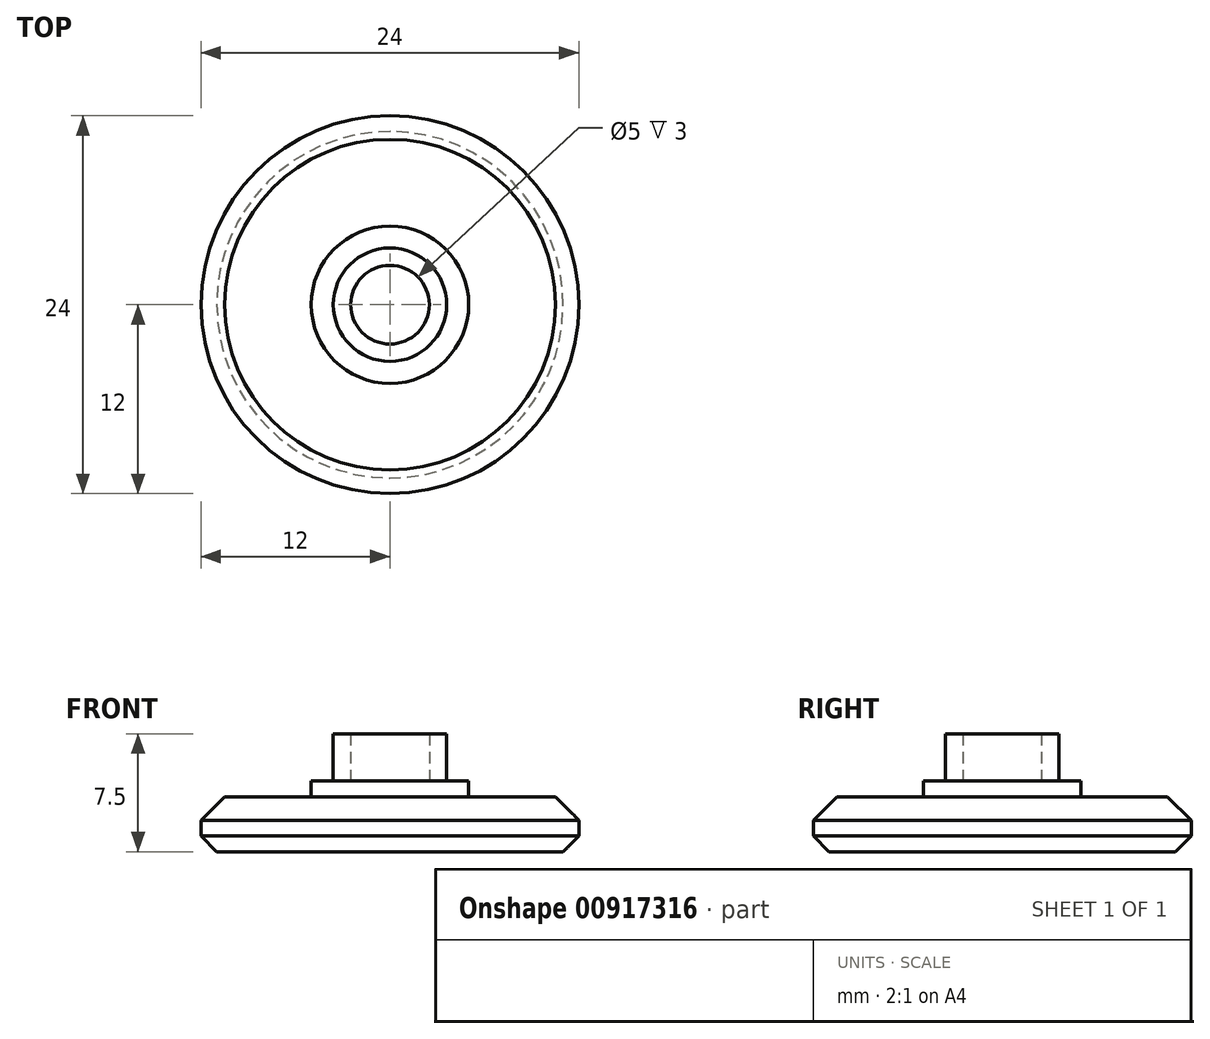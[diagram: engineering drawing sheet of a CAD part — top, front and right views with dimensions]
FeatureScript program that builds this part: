
annotation { "Feature Type Name" : "Feature", "Feature Type Description" : "" }
export const myFeature = defineFeature(function(context is Context, id is Id, definition is map)
    precondition{}
    {
        {
            var Q0;
            Q0=qCreatedBy(makeId("Top.planeOp"),FACE);
            var sketch = newSketch(context, id + "F0", { "sketchPlane" : qUnion([Q0])});
            skCircle(sketch, "E0", {"center": v(0, 0) * mm, "radius": 12 * mm});
            skCircle(sketch, "E1", {"center": v(0, 0) * mm, "radius": 11 * mm});
            skCircle(sketch, "E2", {"center": v(0, 0) * mm, "radius": 4.1 * mm});
            skCircle(sketch, "E3", {"center": v(0, 0) * mm, "radius": 3 * mm});
            skCircle(sketch, "E4", {"center": v(0, 0) * mm, "radius": 5 * mm});
            skSolve(sketch);
        }
        {
            var Q0;
            Q0=makeQuery(id+"F0.imprint","IMPRINT",FACE,{"disambiguationData":[TD([[makeQuery(id+"F0.imprint","IMPRINT",EDGE,{"derivedFrom":sQuery(id+"F0.wireOp",EDGE,"E0")}),1.0]])]});
            var Q1;
            Q1=makeQuery(id+"F0.imprint","IMPRINT",FACE,{"disambiguationData":[TD([[makeQuery(id+"F0.imprint","IMPRINT",EDGE,{"derivedFrom":sQuery(id+"F0.wireOp",EDGE,"E1")}),1.0]])]});
            var Q2;
            Q2=makeQuery(id+"F0.imprint","IMPRINT",FACE,{"disambiguationData":[TD([[makeQuery(id+"F0.imprint","IMPRINT",EDGE,{"derivedFrom":sQuery(id+"F0.wireOp",EDGE,"E3")}),1.0]])]});
            var Q3;
            Q3=makeQuery(id+"F0.imprint","IMPRINT",FACE,{"disambiguationData":[TD([[makeQuery(id+"F0.imprint","IMPRINT",EDGE,{"derivedFrom":sQuery(id+"F0.wireOp",EDGE,"E2")}),1.0]])]});
            var Q4;
            Q4=makeQuery(id+"F0.imprint","IMPRINT",FACE,{"disambiguationData":[TD([[makeQuery(id+"F0.imprint","IMPRINT",EDGE,{"derivedFrom":sQuery(id+"F0.wireOp",EDGE,"E2")}),-1.0]])]});
            extrude(context, id + "F1", {"entities" : qUnion([Q0, Q1, Q2, Q3, Q4]), "depth" : 2 * mm, "offsetDistance" : 25 * mm});
        }
        {
            var Q0;
            Q0=makeQuery(id+"F0.imprint","IMPRINT",FACE,{"disambiguationData":[TD([[makeQuery(id+"F0.imprint","IMPRINT",EDGE,{"derivedFrom":sQuery(id+"F0.wireOp",EDGE,"E1")}),1.0]])]});
            var Q1;
            Q1=makeQuery(id+"F0.imprint","IMPRINT",FACE,{"disambiguationData":[TD([[makeQuery(id+"F0.imprint","IMPRINT",EDGE,{"derivedFrom":sQuery(id+"F0.wireOp",EDGE,"E2")}),1.0]])]});
            var Q2;
            Q2=makeQuery(id+"F0.imprint","IMPRINT",FACE,{"disambiguationData":[TD([[makeQuery(id+"F0.imprint","IMPRINT",EDGE,{"derivedFrom":sQuery(id+"F0.wireOp",EDGE,"E3")}),1.0]])]});
            var Q3;
            Q3=makeQuery(id+"F0.imprint","IMPRINT",FACE,{"disambiguationData":[TD([[makeQuery(id+"F0.imprint","IMPRINT",EDGE,{"derivedFrom":sQuery(id+"F0.wireOp",EDGE,"E2")}),-1.0]])]});
            extrude(context, id + "F2", {"entities" : qUnion([Q0, Q1, Q2, Q3]), "operationType" : NewBodyOperationType.ADD, "depth" : 3.5 * mm, "offsetDistance" : 25 * mm});
        }
        {
            var Q0;
            Q0=makeQuery(id+"F2.boolean.opBoolean","INTERSECT",EDGE,{"derivedFrom":[makeQuery(id+"F1.opExtrude","CAP_FACE",FACE,{"disambiguationData":[OSD([sQuery(id+"F0.wireOp",EDGE,"E0")])],"isStart":false}),makeQuery(id+"F2.opExtrude","SWEPT_FACE",FACE,{"disambiguationData":[OSD([sQuery(id+"F0.wireOp",EDGE,"E1")])]})]});
            chamfer(context, id + "F3", {"entities" : qUnion([Q0]), "width" : 1 * mm, "tangentPropagation" : true});
        }
        {
            var Q0;
            Q0=makeQuery(id+"F0.imprint","IMPRINT",FACE,{"disambiguationData":[TD([[makeQuery(id+"F0.imprint","IMPRINT",EDGE,{"derivedFrom":sQuery(id+"F0.wireOp",EDGE,"E3")}),1.0]])]});
            var Q1;
            Q1=makeQuery(id+"F0.imprint","IMPRINT",FACE,{"disambiguationData":[TD([[makeQuery(id+"F0.imprint","IMPRINT",EDGE,{"derivedFrom":sQuery(id+"F0.wireOp",EDGE,"E2")}),1.0]])]});
            var Q2;
            Q2=makeQuery(id+"F0.imprint","IMPRINT",FACE,{"disambiguationData":[TD([[makeQuery(id+"F0.imprint","IMPRINT",EDGE,{"derivedFrom":sQuery(id+"F0.wireOp",EDGE,"E2")}),-1.0]])]});
            extrude(context, id + "F4", {"entities" : qUnion([Q0, Q1, Q2]), "operationType" : NewBodyOperationType.ADD, "depth" : 4.5 * mm, "offsetDistance" : 25 * mm});
        }
        {
            var Q0;
            Q0=makeQuery(id+"F0.imprint","IMPRINT",FACE,{"disambiguationData":[TD([[makeQuery(id+"F0.imprint","IMPRINT",EDGE,{"derivedFrom":sQuery(id+"F0.wireOp",EDGE,"E2")}),1.0]])]});
            extrude(context, id + "F5", {"entities" : qUnion([Q0]), "operationType" : NewBodyOperationType.ADD, "depth" : 7.5 * mm, "offsetDistance" : 25 * mm});
        }
        {
            var Q0;
            Q0=makeQuery(id+"F1.opExtrude","CAP_EDGE",EDGE,{"disambiguationData":[OSD([sQuery(id+"F0.wireOp",EDGE,"E0")])],"isStart":true});
            chamfer(context, id + "F6", {"entities" : qUnion([Q0]), "width" : 1 * mm, "tangentPropagation" : true});
        }
        {
            var Q0;
            Q0=makeQuery(id+"F2.opExtrude","CAP_EDGE",EDGE,{"disambiguationData":[OSD([sQuery(id+"F0.wireOp",EDGE,"E1")])],"isStart":false});
            chamfer(context, id + "F7", {"entities" : qUnion([Q0]), "width" : 0.5 * mm, "tangentPropagation" : true});
        }
        {
            var Q0;
            Q0=makeQuery(id+"F5.boolean.opBoolean","SPLIT",FACE,{"disambiguationData":[TD([makeQuery(id+"F5.opExtrude","SWEPT_FACE",FACE,{"disambiguationData":[OSD([sQuery(id+"F0.wireOp",EDGE,"E3")])]})])],"derivedFrom":makeQuery(id+"F4.opExtrude","CAP_FACE",FACE,{"disambiguationData":[OSD([sQuery(id+"F0.wireOp",EDGE,"E4")])],"isStart":false})});
            var sketch = newSketch(context, id + "F8", { "sketchPlane" : qUnion([Q0])});
            skCircle(sketch, "E5.0", {"center": v(0, 0) * mm, "radius": 3 * mm});
            skCircle(sketch, "E6.0", {"center": v(0, 0) * mm, "radius": 2.5 * mm});
            skSolve(sketch);
        }
        {
            var Q0;
            Q0=qSketchRegion(id+"F8",true);
            var Q1;
            Q1=makeQuery(id+"F5.opExtrude","CAP_FACE",FACE,{"disambiguationData":[OSD([sQuery(id+"F0.wireOp",EDGE,"E2"),sQuery(id+"F0.wireOp",EDGE,"E3")])],"isStart":false});
            extrude(context, id + "F9", {"entities" : qUnion([Q0]), "operationType" : NewBodyOperationType.ADD, "endBound" : BoundingType.UP_TO_SURFACE, "depth" : 25 * mm, "endBoundEntityFace" : qUnion([Q1]), "offsetDistance" : 25 * mm});
        }
        {
            var Q0;
            Q0=makeQuery(id+"F9.boolean.opBoolean","MERGE",FACE,{"derivedFrom":[makeQuery(id+"F5.opExtrude","CAP_FACE",FACE,{"disambiguationData":[OSD([sQuery(id+"F0.wireOp",EDGE,"E2"),sQuery(id+"F0.wireOp",EDGE,"E3")])],"isStart":false}),makeQuery(id+"F9.opExtrude","CAP_FACE",FACE,{"disambiguationData":[OSD([sQuery(id+"F8.wireOp",EDGE,"E5.0"),sQuery(id+"F8.wireOp",EDGE,"E6.0")])],"isStart":false})]});
            var sketch = newSketch(context, id + "F10", { "sketchPlane" : qUnion([Q0])});
            skCircle(sketch, "E7.0", {"center": v(0, 0) * mm, "radius": 4.1 * mm});
            skCircle(sketch, "E8.0", {"center": v(0, 0) * mm, "radius": 3.6 * mm});
            skSolve(sketch);
        }
        {
            var Q0;
            Q0=qSketchRegion(id+"F10",true);
            var Q1;
            {var subQ0=sQuery(id+"F0.wireOp",EDGE,"E4");Q1=makeQuery(id+"F5.boolean.opBoolean","SPLIT",FACE,{"disambiguationData":[TD([makeQuery(id+"F4.opExtrude","SWEPT_FACE",FACE,{"disambiguationData":[OSD([subQ0])]})])],"derivedFrom":makeQuery(id+"F4.opExtrude","CAP_FACE",FACE,{"disambiguationData":[OSD([subQ0])],"isStart":false})});}
            extrude(context, id + "F11", {"entities" : qUnion([Q0]), "operationType" : NewBodyOperationType.REMOVE, "endBound" : BoundingType.UP_TO_SURFACE, "oppositeDirection" : true, "depth" : 25 * mm, "endBoundEntityFace" : qUnion([Q1]), "offsetDistance" : 25 * mm});
        }
    });
